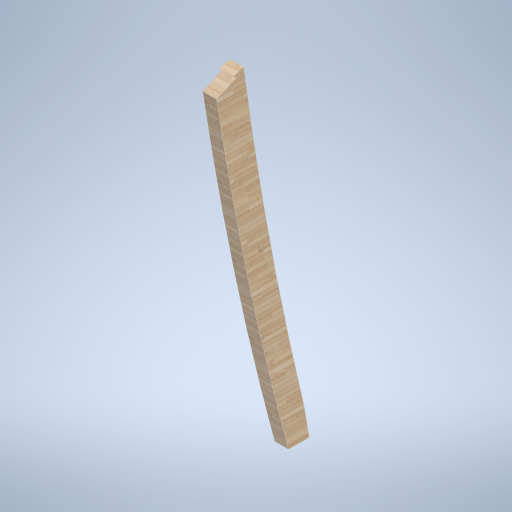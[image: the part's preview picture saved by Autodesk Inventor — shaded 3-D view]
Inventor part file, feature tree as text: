
AUTODESK INVENTOR PART (.ipt)
format: ipt  version: 2024.2 (Build 282272000, 272)  size: 311,296 bytes
history: native  units: in
note: dims shown in document units (in); Inventor stores cm internally (conversion verified against a paired STEP export)
features: other x3, sketch x1
ambient origin geometry x8: Origin, YZ Plane, XZ Plane, XY Plane, X Axis, Y Axis, Z Axis, Center Point
bodies: Solid1 (feature_tree)
feature tree (4):
  other  "side_curve_beam_02_MIR.ipt"
  other  "Solid1::side_curve_beam_02_MIR.ipt"
  other  "TaggingFeature1"
  sketch  "Sketch1"  dims[d0=0.3937in]
